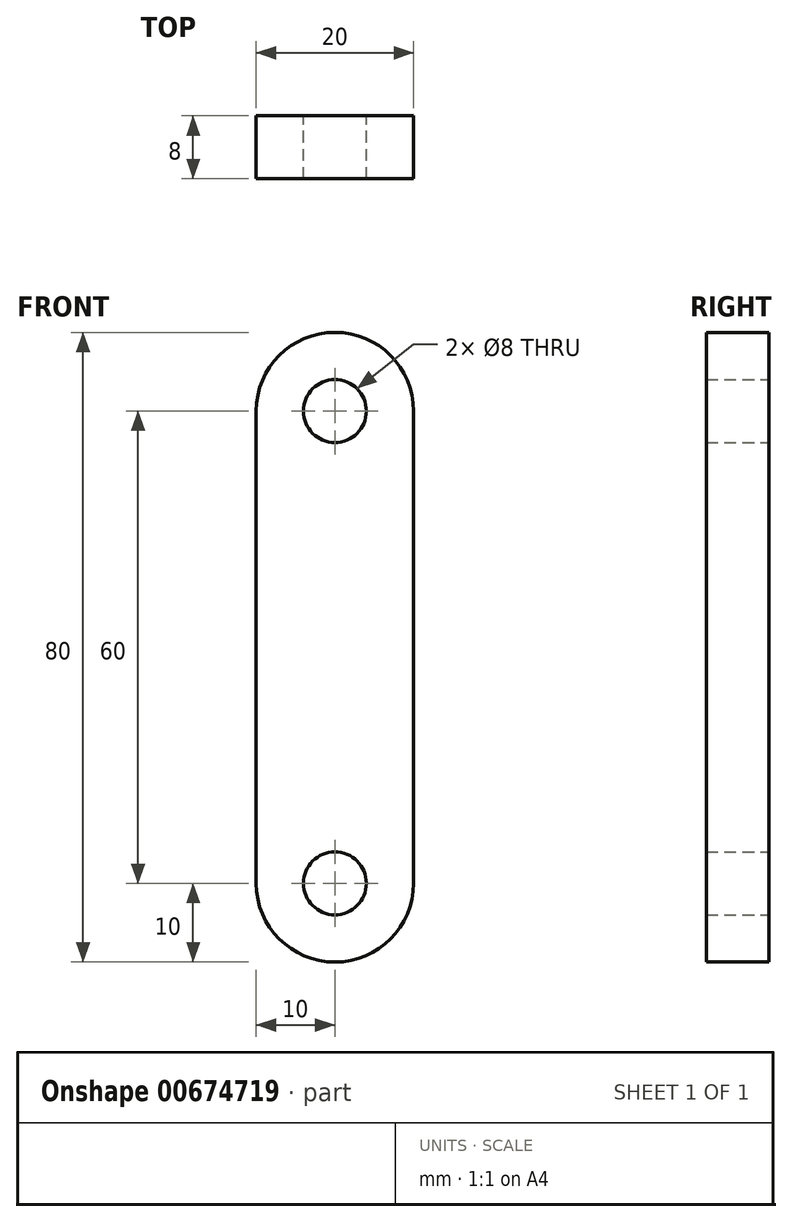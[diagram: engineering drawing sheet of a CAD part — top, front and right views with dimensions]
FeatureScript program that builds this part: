
annotation { "Feature Type Name" : "Feature", "Feature Type Description" : "" }
export const myFeature = defineFeature(function(context is Context, id is Id, definition is map)
    precondition{}
    {
        {
            var Q0;
            Q0=qCreatedBy(makeId("Front.planeOp"),FACE);
            var sketch = newSketch(context, id + "F0", { "sketchPlane" : qUnion([Q0])});
            skCircle(sketch, "E0", {"center": v(0, 0) * mm, "radius": 10 * mm});
            skCircle(sketch, "E1", {"center": v(0, 0) * mm, "radius": 4 * mm});
            skCircle(sketch, "E2", {"center": v(0, 60) * mm, "radius": 10 * mm});
            skCircle(sketch, "E3", {"center": v(0, 60) * mm, "radius": 4 * mm});
            skLineSegment(sketch, "E4", {"start": v(-10, 60) * mm, "end": v(-10, 0) * mm});
            skLineSegment(sketch, "E5", {"start": v(10, 60) * mm, "end": v(10, 0) * mm});
            skSolve(sketch);
        }
        {
            var Q0;
            Q0 = qSketchRegion(id + "F0", true);
            extrude(context, id + "F1", {"entities" : qUnion([Q0]), "depth" : 8 * mm, "offsetDistance" : 25 * mm});
        }
    });
